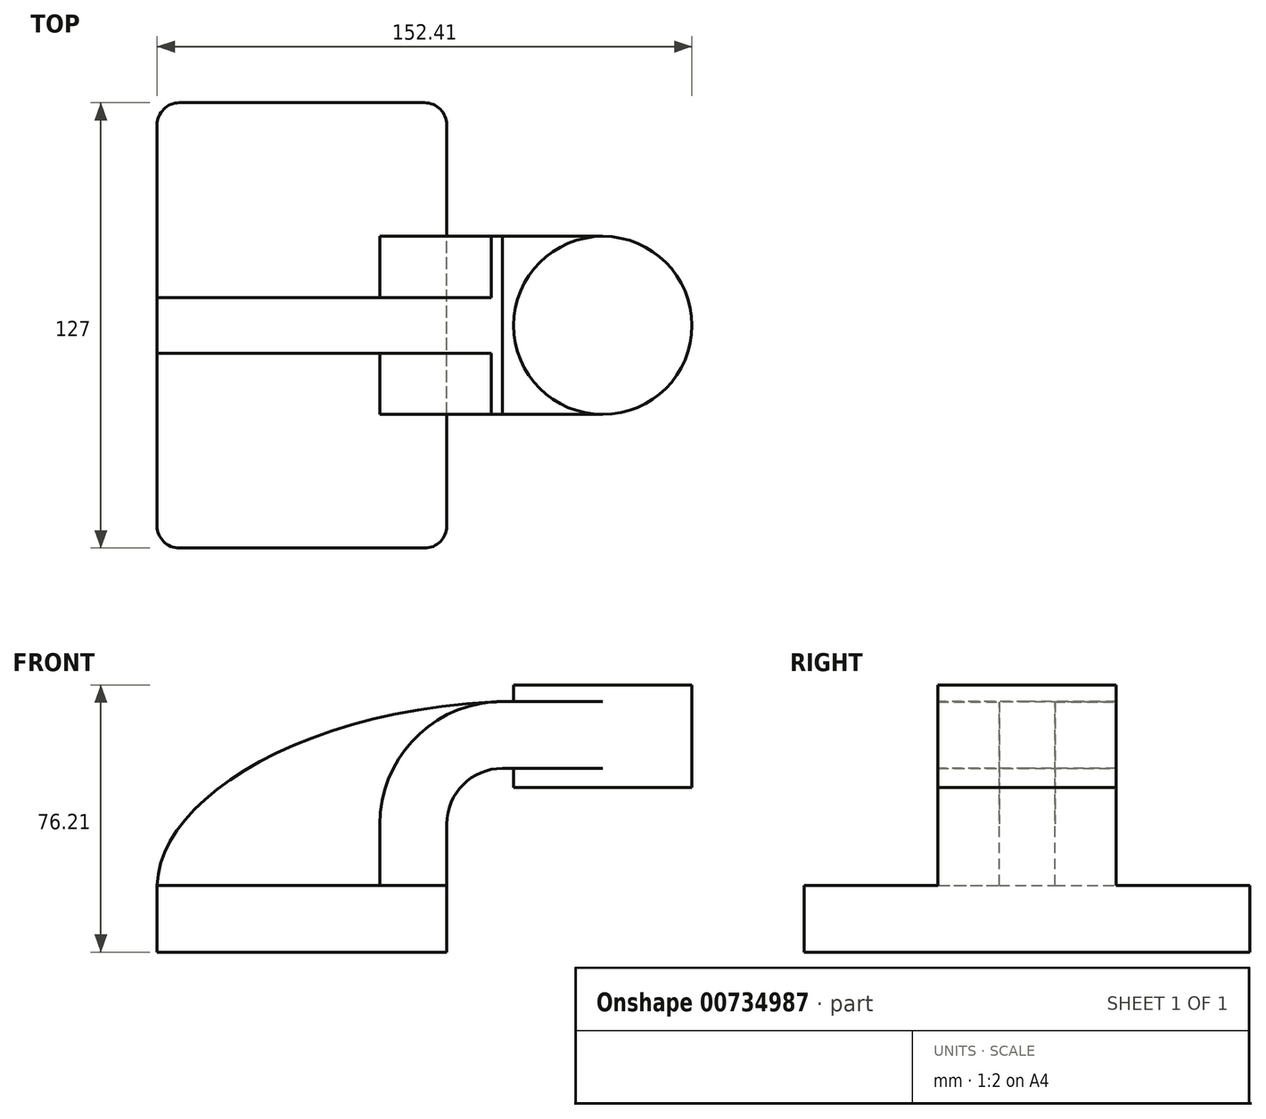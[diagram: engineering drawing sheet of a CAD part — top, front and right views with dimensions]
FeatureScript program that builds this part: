
annotation { "Feature Type Name" : "Feature", "Feature Type Description" : "" }
export const myFeature = defineFeature(function(context is Context, id is Id, definition is map)
    precondition{}
    {
        {
            var Q0;
            Q0=qCreatedBy(makeId("Front.planeOp"),FACE);
            var sketch = newSketch(context, id + "F0", { "sketchPlane" : qUnion([Q0])});
            skLineSegment(sketch, "E0.bottom", {"start": v(-41.28, -9.53) * mm, "end": v(41.28, -9.53) * mm});
            skLineSegment(sketch, "E0.top", {"start": v(-41.28, 9.53) * mm, "end": v(41.28, 9.53) * mm});
            skLineSegment(sketch, "E0.left", {"start": v(-41.28, -9.53) * mm, "end": v(-41.28, 9.53) * mm});
            skLineSegment(sketch, "E0.right", {"start": v(41.28, -9.53) * mm, "end": v(41.28, 9.53) * mm});
            skPoint(sketch, "E0.middle", {"position": v(0, 0) * mm});
            skLineSegment(sketch, "E1.bottom", {"start": v(111.12, 66.68) * mm, "end": v(60.32, 66.68) * mm});
            skLineSegment(sketch, "E1.top", {"start": v(111.12, 37.38) * mm, "end": v(60.33, 37.38) * mm});
            skLineSegment(sketch, "E1.left", {"start": v(111.12, 66.68) * mm, "end": v(111.12, 37.38) * mm});
            skLineSegment(sketch, "E1.right", {"start": v(60.32, 66.68) * mm, "end": v(60.33, 37.38) * mm});
            skPoint(sketch, "E1.middle", {"position": v(85.72, 52.03) * mm});
            skLineSegment(sketch, "E2", {"start": v(41.28, 9.53) * mm, "end": v(41.28, 27) * mm});
            skArc(sketch, "E3", {"start": v(41.27, 27) * mm, "mid": v(45.92, 38.23) * mm, "end": v(57.15, 42.88) * mm});
            skLineSegment(sketch, "E4", {"start": v(57.15, 42.88) * mm, "end": v(85.72, 42.88) * mm});
            skLineSegment(sketch, "E5.0", {"start": v(57.15, 61.93) * mm, "end": v(85.72, 61.93) * mm});
            skArc(sketch, "E5.1", {"start": v(22.22, 27) * mm, "mid": v(32.45, 51.7) * mm, "end": v(57.15, 61.93) * mm});
            skLineSegment(sketch, "E5.2", {"start": v(22.22, 9.53) * mm, "end": v(22.22, 27) * mm});
            skLineSegment(sketch, "E6", {"start": v(85.72, 37.38) * mm, "end": v(85.72, 66.68) * mm});
            skFitSpline(sketch, "E7", {"points": [v(-41.28, 9.53) * mm, v(57.15, 61.93) * mm], "startDerivative": vector(1.63, 73.37) * mm, "endDerivative": vector(171.45, 6.5) * mm});
            skSolve(sketch);
        }
        {
            var Q0;
            Q0=makeQuery(id+"F0.imprint","IMPRINT",FACE,{"disambiguationData":[TD([[makeQuery(id+"F0.imprint","IMPRINT",EDGE,{"derivedFrom":sQuery(id+"F0.wireOp",EDGE,"E0.bottom")}),1.0]])]});
            extrude(context, id + "F1", {"entities" : qUnion([Q0]), "endBound" : BoundingType.SYMMETRIC, "depth" : 127 * mm, "offsetDistance" : 25.4 * mm});
        }
        {
            var Q0;
            {var subQ1=sQuery(id+"F0.wireOp",EDGE,"E2");Q0=makeQuery(id+"F0.imprint","IMPRINT",FACE,{"disambiguationData":[TD([[makeQuery(id+"F0.imprint","IMPRINT",EDGE,{"derivedFrom":subQ1}),1.0]])]});}
            var Q1;
            {var subQ0=sQuery(id+"F0.wireOp",EDGE,"E5.0");var subQ1=sQuery(id+"F0.wireOp",EDGE,"E1.right");var subQ2=makeQuery(id+"F0.imprint","INTERSECT",VERTEX,{"derivedFrom":[subQ1,subQ0]});Q1=makeQuery(id+"F0.imprint","IMPRINT",FACE,{"disambiguationData":[TD([[makeQuery(id+"F0.imprint","IMPRINT",EDGE,{"disambiguationData":[TD([[subQ2,-1.0]])],"derivedFrom":subQ1}),1.0]])]});}
            extrude(context, id + "F2", {"entities" : qUnion([Q0, Q1]), "operationType" : NewBodyOperationType.ADD, "endBound" : BoundingType.SYMMETRIC, "depth" : 50.8 * mm, "offsetDistance" : 25.4 * mm});
        }
        {
            var Q0;
            {var subQ3=sQuery(id+"F0.wireOp",EDGE,"E5.2");Q0=makeQuery(id+"F0.imprint","IMPRINT",FACE,{"disambiguationData":[TD([[makeQuery(id+"F0.imprint","IMPRINT",EDGE,{"derivedFrom":subQ3}),1.0]])]});}
            extrude(context, id + "F3", {"entities" : qUnion([Q0]), "operationType" : NewBodyOperationType.ADD, "endBound" : BoundingType.SYMMETRIC, "depth" : 15.88 * mm, "offsetDistance" : 25.4 * mm});
        }
        {
            var Q0;
            {var subQ0=sQuery(id+"F0.wireOp",EDGE,"E1.left");Q0=makeQuery(id+"F0.imprint","IMPRINT",FACE,{"disambiguationData":[TD([[makeQuery(id+"F0.imprint","IMPRINT",EDGE,{"derivedFrom":subQ0}),-1.0]])]});}
            var Q1;
            Q1=sQuery(id+"F0.wireOp",EDGE,"E6");
            revolve(context, id + "F4", {"operationType" : NewBodyOperationType.ADD, "surfaceOperationType" : NewSurfaceOperationType.NEW, "entities" : qUnion([Q0]), "axis" : qUnion([Q1]), "revolveType" : RevolveType.FULL});
        }
        {
            var Q0;
            Q0=makeQuery(id+"F1.opExtrude","CAP_EDGE",EDGE,{"disambiguationData":[OSD([sQuery(id+"F0.wireOp",EDGE,"E0.left")])],"isStart":false});
            var Q1;
            Q1=makeQuery(id+"F1.opExtrude","CAP_EDGE",EDGE,{"disambiguationData":[OSD([sQuery(id+"F0.wireOp",EDGE,"E0.right")])],"isStart":false});
            var Q2;
            Q2=makeQuery(id+"F1.opExtrude","CAP_EDGE",EDGE,{"disambiguationData":[OSD([sQuery(id+"F0.wireOp",EDGE,"E0.right")])],"isStart":true});
            var Q3;
            Q3=makeQuery(id+"F1.opExtrude","CAP_EDGE",EDGE,{"disambiguationData":[OSD([sQuery(id+"F0.wireOp",EDGE,"E0.left")])],"isStart":true});
            fillet(context, id + "F5", {"entities" : qUnion([Q0, Q1, Q2, Q3]), "radius" : 6.35 * mm, "tangentPropagation" : true, "allowEdgeOverflow" : false});
        }
    });
